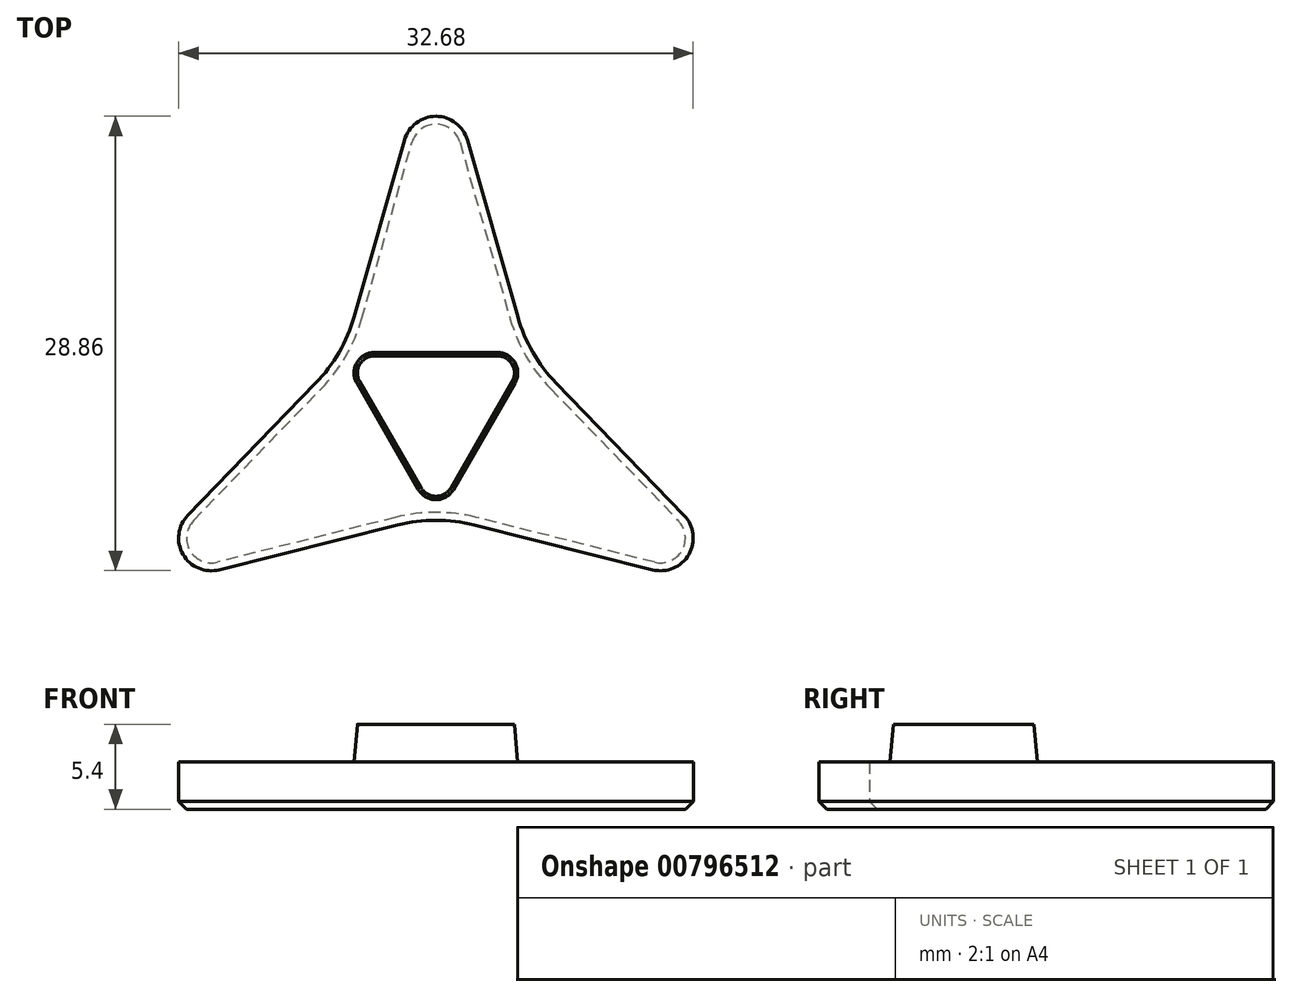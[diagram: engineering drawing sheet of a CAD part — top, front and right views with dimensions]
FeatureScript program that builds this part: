
annotation { "Feature Type Name" : "Feature", "Feature Type Description" : "" }
export const myFeature = defineFeature(function(context is Context, id is Id, definition is map)
    precondition{}
    {
        {
            var Q0;
            Q0=qCreatedBy(makeId("Top.planeOp"),FACE);
            var sketch = newSketch(context, id + "F0", { "sketchPlane" : qUnion([Q0])});
            skCircle(sketch, "E0.cCircle", {"center": v(0, 0) * mm, "radius": 3.55 * mm, "construction": true});
            skLineSegment(sketch, "E0.0", {"start": v(-3.9, 3.55) * mm, "end": v(3.9, 3.55) * mm});
            skLineSegment(sketch, "E0.1", {"start": v(5.02, 1.6) * mm, "end": v(1.13, -5.15) * mm});
            skLineSegment(sketch, "E0.2", {"start": v(-1.13, -5.15) * mm, "end": v(-5.02, 1.6) * mm});
            skPoint(sketch, "E0.0.midPoint", {"position": v(0, 3.55) * mm});
            skPoint(sketch, "E1.visualSharp", {"position": v(0, -7.1) * mm});
            skArc(sketch, "E1.filletArc", {"start": v(-1.13, -5.15) * mm, "mid": v(0, -5.8) * mm, "end": v(1.13, -5.15) * mm});
            skPoint(sketch, "E2.visualSharp", {"position": v(-6.15, 3.55) * mm});
            skArc(sketch, "E2.filletArc", {"start": v(-3.9, 3.55) * mm, "mid": v(-5.02, 2.9) * mm, "end": v(-5.02, 1.6) * mm});
            skPoint(sketch, "E3.visualSharp", {"position": v(6.15, 3.55) * mm});
            skArc(sketch, "E3.filletArc", {"start": v(5.02, 1.6) * mm, "mid": v(5.02, 2.9) * mm, "end": v(3.9, 3.55) * mm});
            skSolve(sketch);
        }
        {
            var Q0;
            Q0=makeQuery(id+"F0.imprint","IMPRINT",FACE,{"disambiguationData":[TD([[makeQuery(id+"F0.imprint","IMPRINT",EDGE,{"derivedFrom":sQuery(id+"F0.wireOp",EDGE,"E0.0")}),-1.0]])]});
            extrude(context, id + "F1", {"entities" : qUnion([Q0]), "depth" : 2.4 * mm, "offsetDistance" : 25 * mm, "hasDraft" : true, "draftAngle" : 5 * degree, "draftPullDirection" : true});
        }
        {
            var Q0;
            Q0=makeQuery(id+"F1.opExtrude","CAP_FACE",FACE,{"disambiguationData":[OSD([sQuery(id+"F0.wireOp",EDGE,"E0.0"),sQuery(id+"F0.wireOp",EDGE,"E0.1"),sQuery(id+"F0.wireOp",EDGE,"E0.2"),sQuery(id+"F0.wireOp",EDGE,"E1.filletArc"),sQuery(id+"F0.wireOp",EDGE,"E2.filletArc"),sQuery(id+"F0.wireOp",EDGE,"E3.filletArc")])],"isStart":true});
            var sketch = newSketch(context, id + "F2", { "sketchPlane" : qUnion([Q0])});
            skLineSegment(sketch, "E4", {"start": v(0, 0) * mm, "end": v(-7.58, -4.38) * mm, "construction": true});
            skLineSegment(sketch, "E5", {"start": v(-5.89, -3.4) * mm, "end": v(-2, -17.04) * mm});
            skLineSegment(sketch, "E6", {"start": v(0, 0) * mm, "end": v(7.45, -4.3) * mm, "construction": true});
            skLineSegment(sketch, "E7", {"start": v(2, -17.04) * mm, "end": v(5.89, -3.4) * mm});
            skPoint(sketch, "E8.visualSharp", {"position": v(0, -24.06) * mm});
            skArc(sketch, "E8.filletArc", {"start": v(-2, -17.04) * mm, "mid": v(0, -18.55) * mm, "end": v(2, -17.04) * mm});
            skLineSegment(sketch, "E9.1.0", {"start": v(5.89, -3.4) * mm, "end": v(15.76, 6.79) * mm});
            skArc(sketch, "E9.1.1", {"start": v(15.76, 6.79) * mm, "mid": v(16.06, 9.27) * mm, "end": v(13.76, 10.25) * mm});
            skLineSegment(sketch, "E9.1.2", {"start": v(13.76, 10.25) * mm, "end": v(0, 6.8) * mm});
            skLineSegment(sketch, "E9.2.0", {"start": v(0, 6.8) * mm, "end": v(-13.76, 10.25) * mm});
            skArc(sketch, "E9.2.1", {"start": v(-13.76, 10.25) * mm, "mid": v(-16.06, 9.27) * mm, "end": v(-15.76, 6.79) * mm});
            skLineSegment(sketch, "E9.2.2", {"start": v(-15.76, 6.79) * mm, "end": v(-5.89, -3.4) * mm});
            skPoint(sketch, "E9.center", {"position": v(0, 0) * mm});
            skSolve(sketch);
        }
        {
            var Q0;
            Q0 = qSketchRegion(id + "F2", true);
            extrude(context, id + "F3", {"entities" : qUnion([Q0]), "operationType" : NewBodyOperationType.ADD, "depth" : 3 * mm, "offsetDistance" : 25 * mm});
        }
        {
            var Q0;
            Q0=makeQuery(id+"F3.opExtrude","SWEPT_EDGE",EDGE,{"disambiguationData":[OSD([sQuery(id+"F2.wireOp",EDGE,"E9.1.2"),sQuery(id+"F2.wireOp",EDGE,"E9.2.0")])]});
            var Q1;
            Q1=makeQuery(id+"F3.opExtrude","SWEPT_EDGE",EDGE,{"disambiguationData":[OSD([sQuery(id+"F2.wireOp",EDGE,"E7"),sQuery(id+"F2.wireOp",EDGE,"E9.1.0")])]});
            var Q2;
            Q2=makeQuery(id+"F3.opExtrude","SWEPT_EDGE",EDGE,{"disambiguationData":[OSD([sQuery(id+"F2.wireOp",EDGE,"E5"),sQuery(id+"F2.wireOp",EDGE,"E9.2.2")])]});
            fillet(context, id + "F4", {"entities" : qUnion([Q0, Q1, Q2]), "radius" : 10 * mm, "tangentPropagation" : true, "allowEdgeOverflow" : false});
        }
        {
            var Q0;
            Q0=makeQuery(id+"F3.opExtrude","CAP_FACE",FACE,{"disambiguationData":[OSD([sQuery(id+"F2.wireOp",EDGE,"E5"),sQuery(id+"F2.wireOp",EDGE,"E7"),sQuery(id+"F2.wireOp",EDGE,"E8.filletArc"),sQuery(id+"F2.wireOp",EDGE,"E9.1.0"),sQuery(id+"F2.wireOp",EDGE,"E9.1.1"),sQuery(id+"F2.wireOp",EDGE,"E9.1.2"),sQuery(id+"F2.wireOp",EDGE,"E9.2.0"),sQuery(id+"F2.wireOp",EDGE,"E9.2.1"),sQuery(id+"F2.wireOp",EDGE,"E9.2.2")])],"isStart":false});
            chamfer(context, id + "F5", {"entities" : qUnion([Q0]), "width" : 0.5 * mm, "tangentPropagation" : true});
        }
    });
